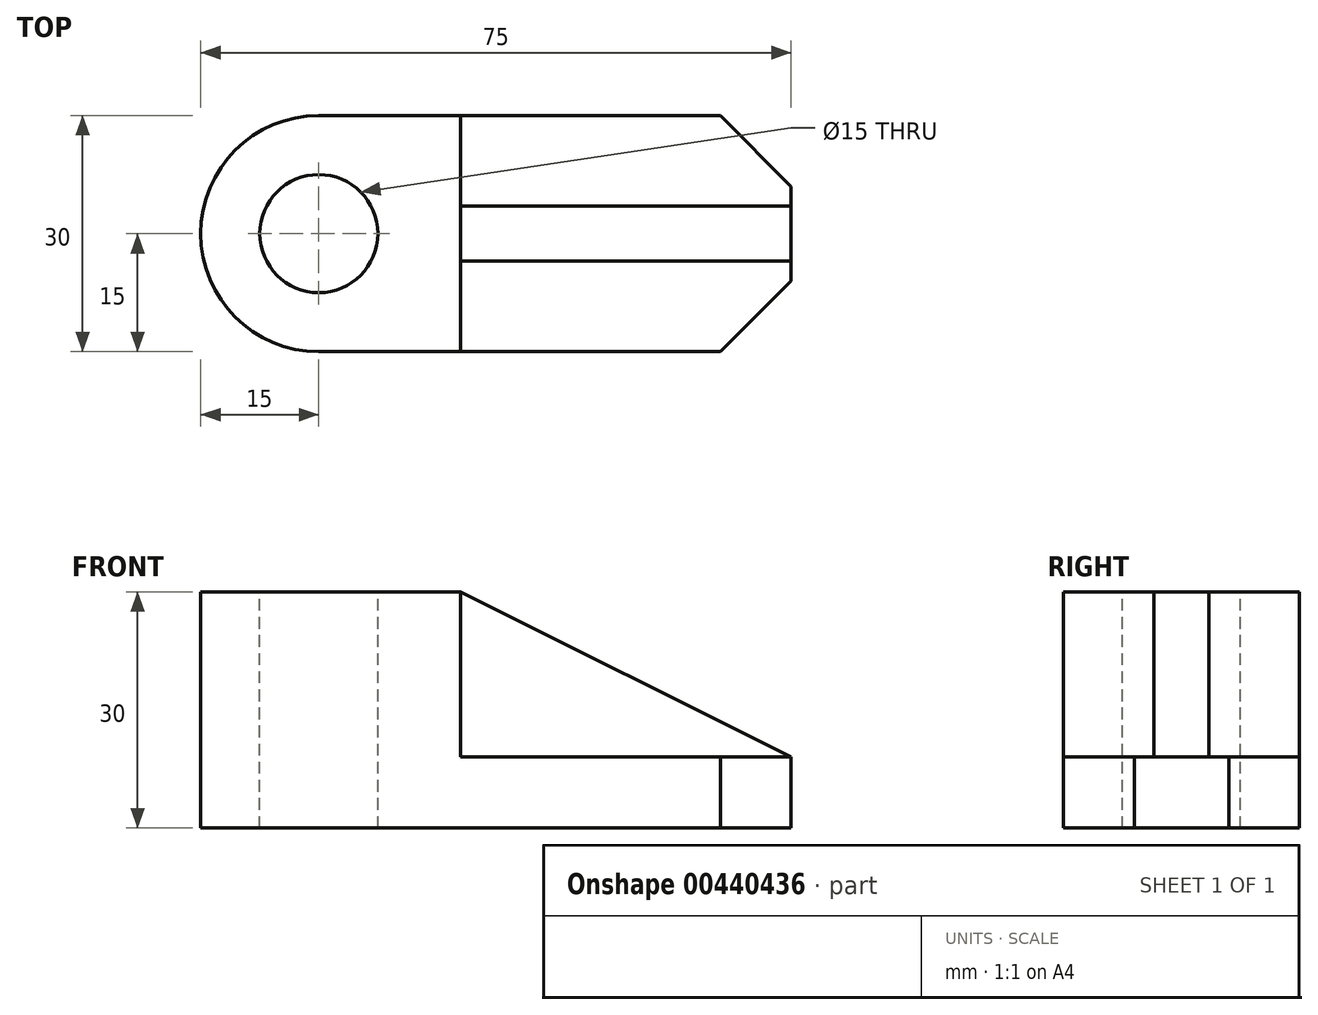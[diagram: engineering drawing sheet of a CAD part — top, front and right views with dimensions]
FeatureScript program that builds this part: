
annotation { "Feature Type Name" : "Feature", "Feature Type Description" : "" }
export const myFeature = defineFeature(function(context is Context, id is Id, definition is map)
    precondition{}
    {
        {
            var Q0;
            Q0=qCreatedBy(makeId("Top.planeOp"),FACE);
            var sketch = newSketch(context, id + "F0", { "sketchPlane" : qUnion([Q0])});
            skLineSegment(sketch, "E0", {"start": v(0, 0) * mm, "end": v(9, 9) * mm});
            skLineSegment(sketch, "E1", {"start": v(9, 9) * mm, "end": v(9, 21) * mm});
            skLineSegment(sketch, "E2", {"start": v(9, 21) * mm, "end": v(0, 30) * mm});
            skLineSegment(sketch, "E3", {"start": v(0, 30) * mm, "end": v(-51, 30) * mm});
            skLineSegment(sketch, "E4", {"start": v(0, 0) * mm, "end": v(-51, 0) * mm});
            skArc(sketch, "E5", {"start": v(-51, 30) * mm, "mid": v(-66, 15) * mm, "end": v(-51, 0) * mm});
            skSolve(sketch);
        }
        {
            var Q0;
            Q0=makeQuery(id+"F0.imprint","IMPRINT",FACE,{"disambiguationData":[TD([[makeQuery(id+"F0.imprint","IMPRINT",EDGE,{"derivedFrom":sQuery(id+"F0.wireOp",EDGE,"E0")}),1.0]])]});
            extrude(context, id + "F1", {"entities" : qUnion([Q0]), "depth" : 9 * mm});
        }
        {
            var Q0;
            Q0=makeQuery(id+"F1.opExtrude","CAP_FACE",FACE,{"disambiguationData":[OSD([sQuery(id+"F0.wireOp",EDGE,"E0"),sQuery(id+"F0.wireOp",EDGE,"E1"),sQuery(id+"F0.wireOp",EDGE,"E2"),sQuery(id+"F0.wireOp",EDGE,"E3"),sQuery(id+"F0.wireOp",EDGE,"E4"),sQuery(id+"F0.wireOp",EDGE,"E5")])],"isStart":false});
            var sketch = newSketch(context, id + "F2", { "sketchPlane" : qUnion([Q0])});
            skLineSegment(sketch, "E6", {"start": v(-33, 30) * mm, "end": v(-33, 18.5) * mm});
            skLineSegment(sketch, "E7", {"start": v(-33, 18.5) * mm, "end": v(9, 18.5) * mm});
            skLineSegment(sketch, "E8", {"start": v(9, 18.5) * mm, "end": v(9, 11.5) * mm});
            skLineSegment(sketch, "E9", {"start": v(9, 11.5) * mm, "end": v(-33, 11.5) * mm});
            skLineSegment(sketch, "E10", {"start": v(-33, 11.5) * mm, "end": v(-33, 0) * mm});
            skLineSegment(sketch, "E11", {"start": v(-33, 0) * mm, "end": v(-51, 0) * mm});
            skLineSegment(sketch, "E12", {"start": v(-33, 30) * mm, "end": v(-51, 30) * mm});
            skArc(sketch, "E13", {"start": v(-51, 30) * mm, "mid": v(-66, 15) * mm, "end": v(-51, 0) * mm});
            skSolve(sketch);
        }
        {
            var Q0;
            Q0=makeQuery(id+"F2.imprint","IMPRINT",FACE,{"disambiguationData":[TD([[makeQuery(id+"F2.imprint","IMPRINT",EDGE,{"derivedFrom":sQuery(id+"F2.wireOp",EDGE,"E6")}),-1.0]])]});
            extrude(context, id + "F3", {"entities" : qUnion([Q0]), "operationType" : NewBodyOperationType.ADD, "depth" : 21 * mm});
        }
        {
            var Q0;
            Q0=makeQuery(id+"F3.opExtrude","CAP_EDGE",EDGE,{"disambiguationData":[OSD([sQuery(id+"F2.wireOp",EDGE,"E8")])],"isStart":false});
            chamfer(context, id + "F4", {"entities" : qUnion([Q0]), "chamferType" : ChamferType.TWO_OFFSETS, "width1" : 42 * mm, "oppositeDirection" : false, "width2" : 21 * mm, "tangentPropagation" : true});
        }
        {
            var Q0;
            Q0=makeQuery(id+"F3.opExtrude","CAP_FACE",FACE,{"disambiguationData":[OSD([sQuery(id+"F2.wireOp",EDGE,"E6"),sQuery(id+"F2.wireOp",EDGE,"E7"),sQuery(id+"F2.wireOp",EDGE,"E8"),sQuery(id+"F2.wireOp",EDGE,"E9"),sQuery(id+"F2.wireOp",EDGE,"E10"),sQuery(id+"F2.wireOp",EDGE,"E11"),sQuery(id+"F2.wireOp",EDGE,"E12"),sQuery(id+"F2.wireOp",EDGE,"E13")])],"isStart":false});
            var sketch = newSketch(context, id + "F5", { "sketchPlane" : qUnion([Q0])});
            skPoint(sketch, "E14", {"position": v(-51, 15) * mm});
            skArc(sketch, "E15.0", {"start": v(-51, 30) * mm, "mid": v(-66, 15) * mm, "end": v(-51, 0) * mm});
            skSolve(sketch);
        }
        {
            var Q0;
            Q0=sQuery(id+"F5.wireOp",VERTEX,"E14");
            var Q1;
            Q1=makeQuery(id+"F1.opExtrude","SWEPT_BODY",BODY,{"disambiguationData":[OSD([sQuery(id+"F0.wireOp",EDGE,"E0"),sQuery(id+"F0.wireOp",EDGE,"E1"),sQuery(id+"F0.wireOp",EDGE,"E2"),sQuery(id+"F0.wireOp",EDGE,"E3"),sQuery(id+"F0.wireOp",EDGE,"E4"),sQuery(id+"F0.wireOp",EDGE,"E5")])]});
            hole(context, id + "F6", {"style" : HoleStyle.SIMPLE, "endStyle" : HoleEndStyle.THROUGH, "holeDiameter" : 15 * mm, "isTappedThrough" : true, "tappedDepth" : 12 * mm, "tapClearance" : 3, "locations" : qUnion([Q0]), "scope" : qUnion([Q1])});
        }
    });
